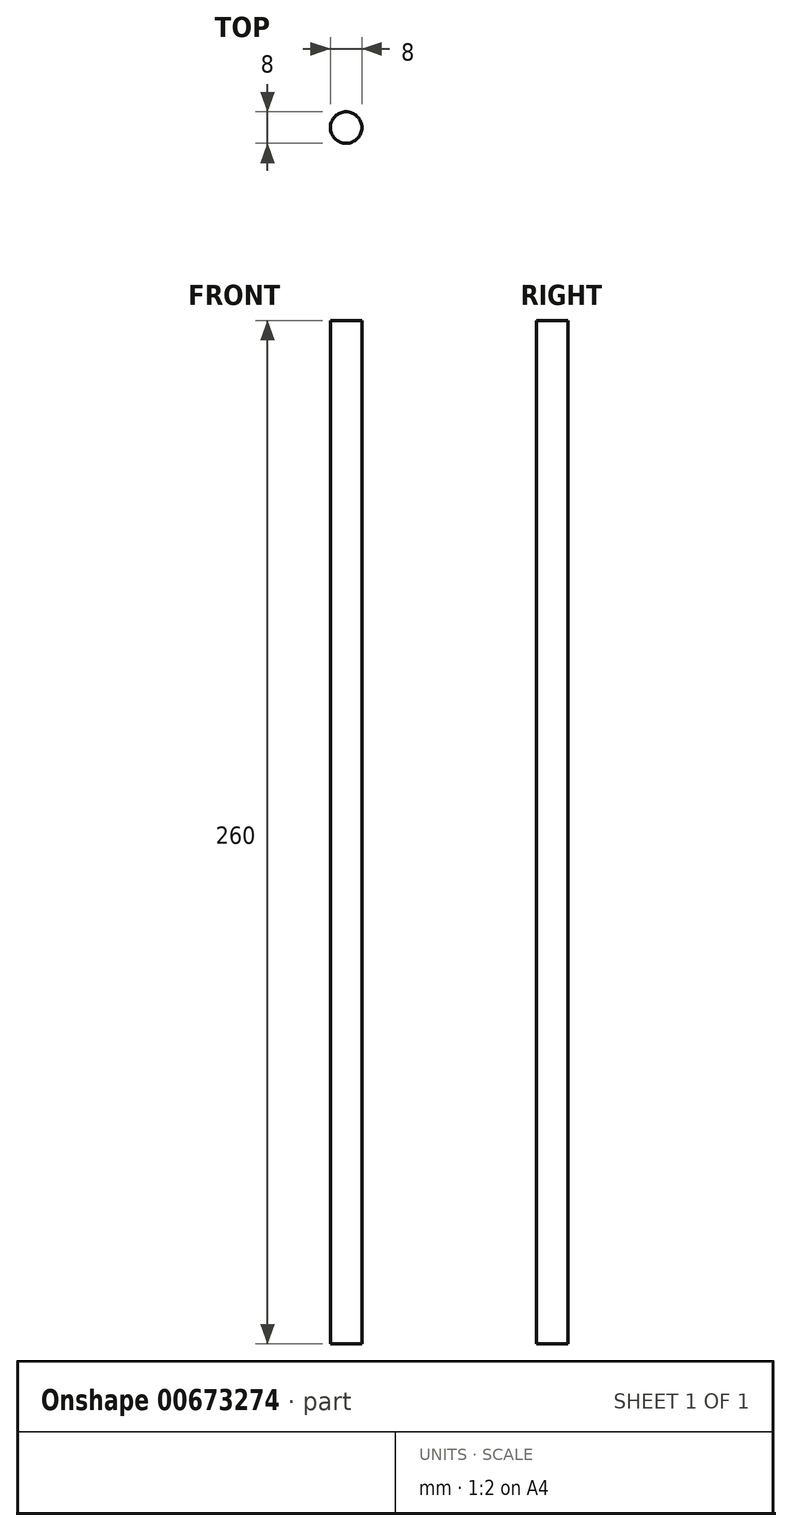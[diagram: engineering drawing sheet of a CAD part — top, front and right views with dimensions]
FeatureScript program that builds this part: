
annotation { "Feature Type Name" : "Feature", "Feature Type Description" : "" }
export const myFeature = defineFeature(function(context is Context, id is Id, definition is map)
    precondition{}
    {
        {
            var Q0;
            Q0=qCreatedBy(makeId("Top.planeOp"),FACE);
            var sketch = newSketch(context, id + "F0", { "sketchPlane" : qUnion([Q0])});
            skCircle(sketch, "E0", {"center": v(0, 0) * mm, "radius": 4 * mm});
            skSolve(sketch);
        }
        {
            var Q0;
            Q0=sQuery(id+"F0.wireOp",EDGE,"E0");
            extrude(context, id + "F1", {"bodyType" : ToolBodyType.SURFACE, "surfaceEntities" : qUnion([Q0]), "depth" : 260 * mm, "offsetDistance" : 25 * mm});
        }
    });
